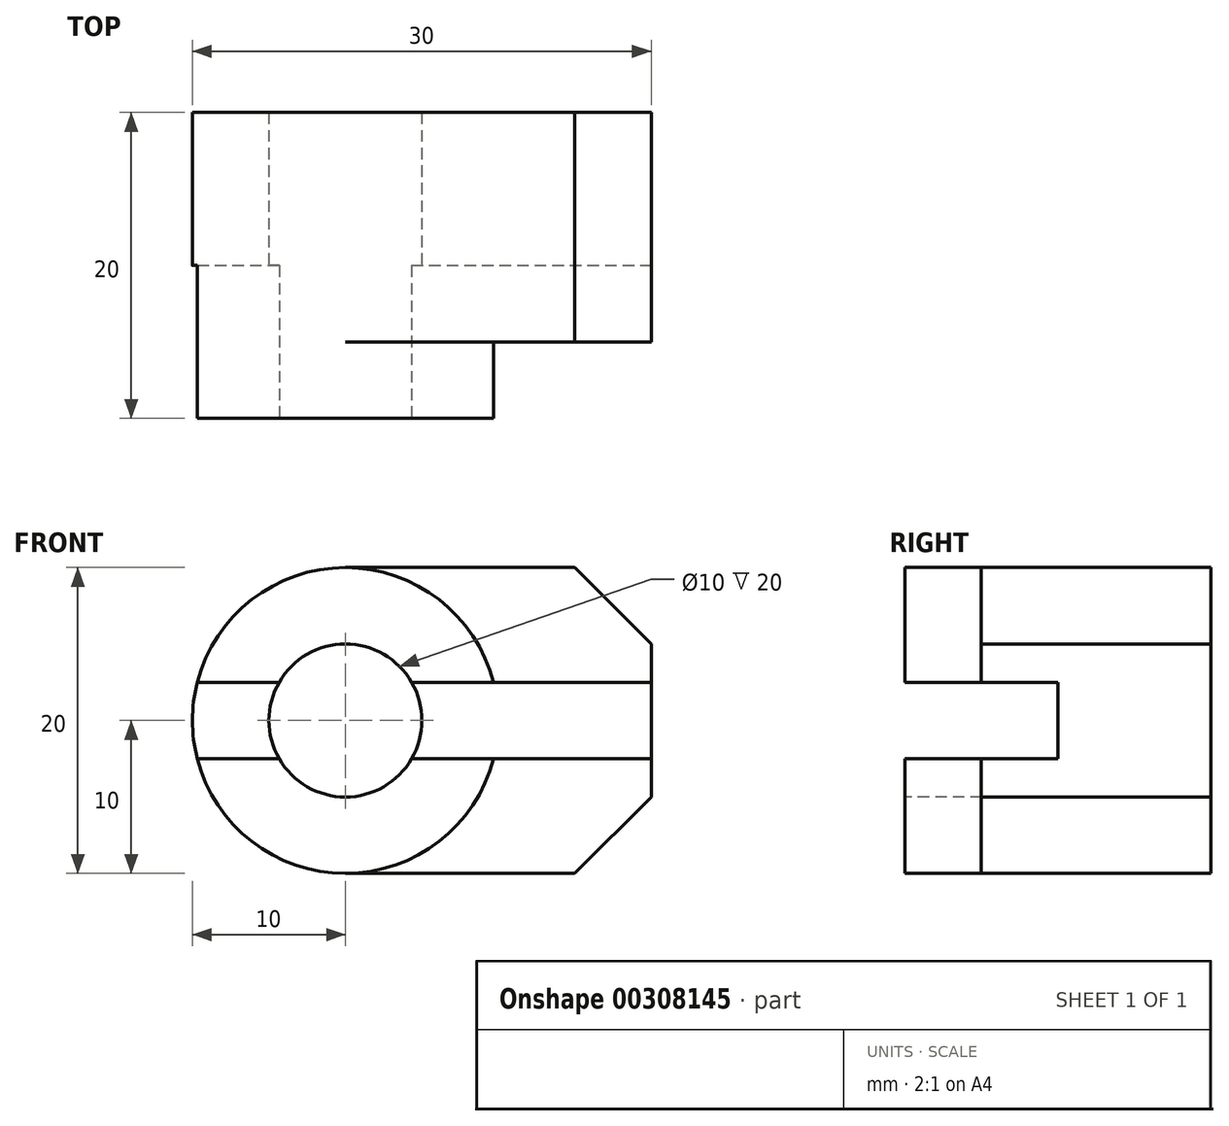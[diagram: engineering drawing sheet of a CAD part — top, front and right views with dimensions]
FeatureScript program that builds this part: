
annotation { "Feature Type Name" : "Feature", "Feature Type Description" : "" }
export const myFeature = defineFeature(function(context is Context, id is Id, definition is map)
    precondition{}
    {
        {
            var Q0;
            Q0=qCreatedBy(makeId("Front.planeOp"),FACE);
            var sketch = newSketch(context, id + "F0", { "sketchPlane" : qUnion([Q0])});
            skCircle(sketch, "E0", {"center": v(0, 0) * mm, "radius": 10 * mm});
            skCircle(sketch, "E1", {"center": v(0, 0) * mm, "radius": 5 * mm});
            skSolve(sketch);
        }
        {
            var Q0;
            Q0 = qSketchRegion(id + "F0", true);
            extrude(context, id + "F1", {"entities" : qUnion([Q0]), "oppositeDirection" : true, "depth" : 20 * mm});
        }
        {
            var Q0;
            Q0=qCreatedBy(makeId("Front.planeOp"),FACE);
            cPlane(context, id + "F2", {"entities" : qUnion([Q0]), "cplaneType" : CPlaneType.OFFSET, "offset" : 5 * mm, "oppositeDirection" : true, "width" : 150 * mm, "height" : 150 * mm});
        }
        {
            var Q0;
            Q0=qCreatedBy(id+"F2.planeOp",FACE);
            var sketch = newSketch(context, id + "F3", { "sketchPlane" : qUnion([Q0])});
            skLineSegment(sketch, "E2", {"start": v(0, 10) * mm, "end": v(0, 5) * mm});
            skArc(sketch, "E3", {"start": v(0, -5) * mm, "mid": v(5, 0) * mm, "end": v(0, 5) * mm});
            skLineSegment(sketch, "E4", {"start": v(0, -5) * mm, "end": v(0, -10) * mm});
            skLineSegment(sketch, "E5", {"start": v(0, 10) * mm, "end": v(15, 10) * mm});
            skLineSegment(sketch, "E6", {"start": v(0, -10) * mm, "end": v(15, -10) * mm});
            skLineSegment(sketch, "E7", {"start": v(15, -10) * mm, "end": v(20, -5) * mm});
            skLineSegment(sketch, "E8", {"start": v(20, -5) * mm, "end": v(20, 5) * mm});
            skLineSegment(sketch, "E9", {"start": v(20, 5) * mm, "end": v(15, 10) * mm});
            skSolve(sketch);
        }
        {
            var Q0;
            Q0 = qSketchRegion(id + "F3", true);
            extrude(context, id + "F4", {"entities" : qUnion([Q0]), "operationType" : NewBodyOperationType.ADD, "oppositeDirection" : true, "depth" : 15 * mm});
        }
        {
            var Q0;
            Q0=makeQuery(id+"F4.opExtrude","SWEPT_FACE",FACE,{"disambiguationData":[OSD([sQuery(id+"F3.wireOp",EDGE,"E8")])]});
            var sketch = newSketch(context, id + "F5", { "sketchPlane" : qUnion([Q0])});
            skLineSegment(sketch, "E10", {"start": v(0, 2.5) * mm, "end": v(10, 2.5) * mm});
            skLineSegment(sketch, "E11", {"start": v(10, 2.5) * mm, "end": v(10, -2.5) * mm});
            skLineSegment(sketch, "E12", {"start": v(10, -2.5) * mm, "end": v(0, -2.5) * mm});
            skLineSegment(sketch, "E13", {"start": v(0, -2.5) * mm, "end": v(0, 2.5) * mm});
            skSolve(sketch);
        }
        {
            var Q0;
            Q0 = qSketchRegion(id + "F5", true);
            extrude(context, id + "F6", {"entities" : qUnion([Q0]), "operationType" : NewBodyOperationType.REMOVE, "oppositeDirection" : true, "depth" : 30 * mm});
        }
    });
